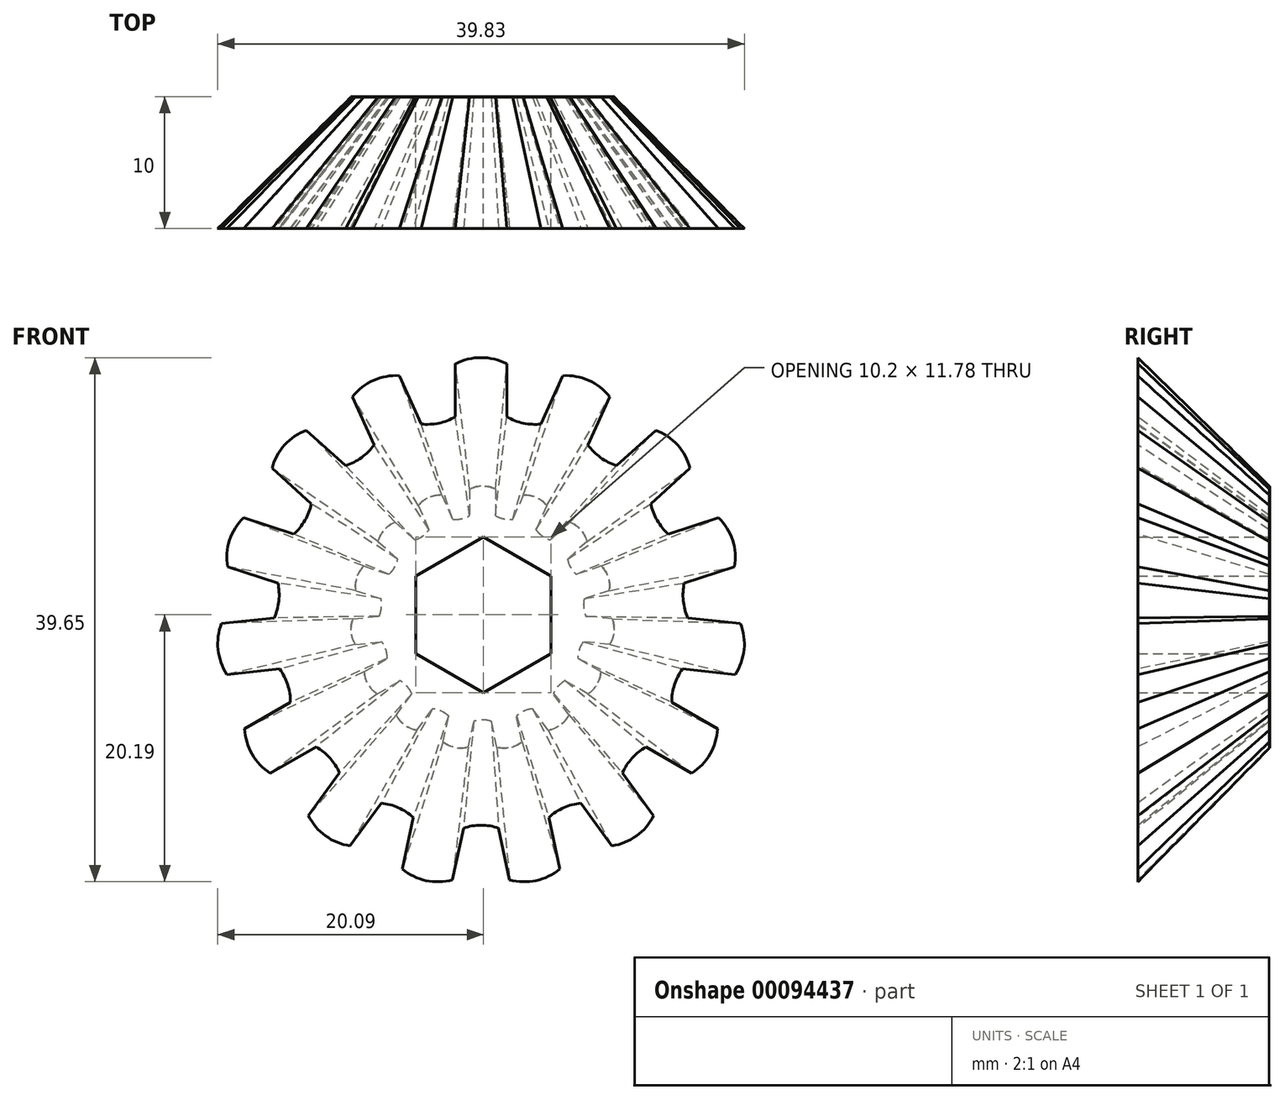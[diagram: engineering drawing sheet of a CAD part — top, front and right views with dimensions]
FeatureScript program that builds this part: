
annotation { "Feature Type Name" : "Feature", "Feature Type Description" : "" }
export const myFeature = defineFeature(function(context is Context, id is Id, definition is map)
    precondition{}
    {
        {
            var Q0;
            Q0=qCreatedBy(makeId("Front.planeOp"),FACE);
            cPlane(context, id + "F0", {"entities" : qUnion([Q0]), "cplaneType" : CPlaneType.OFFSET, "offset" : 10 * mm, "width" : 150 * mm, "height" : 150 * mm});
        }
        {
            var Q0;
            Q0=qCreatedBy(makeId("Front.planeOp"),FACE);
            var sketch = newSketch(context, id + "F1", { "sketchPlane" : qUnion([Q0])});
            skLineSegment(sketch, "E0", {"start": v(-2.07, 19.01) * mm, "end": v(-2.07, 15.01) * mm});
            skLineSegment(sketch, "E1.MirrorCS", {"start": v(1.81, 19.01) * mm, "end": v(1.81, 15.01) * mm});
            skArc(sketch, "E2", {"start": v(1.81, 19.01) * mm, "mid": v(-0.13, 19.49) * mm, "end": v(-2.07, 19.01) * mm});
            skLineSegment(sketch, "E3.1.0", {"start": v(-9.84, 16.54) * mm, "end": v(-8.22, 12.88) * mm});
            skArc(sketch, "E3.1.1", {"start": v(-6.3, 18.12) * mm, "mid": v(-8.26, 17.76) * mm, "end": v(-9.84, 16.54) * mm});
            skLineSegment(sketch, "E3.1.2", {"start": v(-6.3, 18.12) * mm, "end": v(-4.67, 14.46) * mm});
            skLineSegment(sketch, "E3.2.0", {"start": v(-15.94, 11.1) * mm, "end": v(-12.97, 8.43) * mm});
            skArc(sketch, "E3.2.1", {"start": v(-13.34, 14) * mm, "mid": v(-15, 12.87) * mm, "end": v(-15.94, 11.1) * mm});
            skLineSegment(sketch, "E3.2.2", {"start": v(-13.34, 14) * mm, "end": v(-10.37, 11.32) * mm});
            skLineSegment(sketch, "E3.3.0", {"start": v(-19.3, 3.67) * mm, "end": v(-15.5, 2.44) * mm});
            skArc(sketch, "E3.3.1", {"start": v(-18.1, 7.37) * mm, "mid": v(-19.15, 5.67) * mm, "end": v(-19.3, 3.67) * mm});
            skLineSegment(sketch, "E3.3.2", {"start": v(-18.1, 7.37) * mm, "end": v(-14.3, 6.13) * mm});
            skLineSegment(sketch, "E3.4.0", {"start": v(-19.34, -4.49) * mm, "end": v(-15.37, -4.07) * mm});
            skArc(sketch, "E3.4.1", {"start": v(-19.75, -0.62) * mm, "mid": v(-20.02, -2.6) * mm, "end": v(-19.34, -4.49) * mm});
            skLineSegment(sketch, "E3.4.2", {"start": v(-19.75, -0.62) * mm, "end": v(-15.77, -0.2) * mm});
            skLineSegment(sketch, "E3.5.0", {"start": v(-16.07, -11.96) * mm, "end": v(-12.6, -9.96) * mm});
            skArc(sketch, "E3.5.1", {"start": v(-18, -8.6) * mm, "mid": v(-17.45, -10.51) * mm, "end": v(-16.07, -11.96) * mm});
            skLineSegment(sketch, "E3.5.2", {"start": v(-18, -8.6) * mm, "end": v(-14.55, -6.6) * mm});
            skLineSegment(sketch, "E3.6.0", {"start": v(-10.03, -17.45) * mm, "end": v(-7.68, -14.21) * mm});
            skArc(sketch, "E3.6.1", {"start": v(-13.18, -15.17) * mm, "mid": v(-11.88, -16.7) * mm, "end": v(-10.03, -17.45) * mm});
            skLineSegment(sketch, "E3.6.2", {"start": v(-13.18, -15.17) * mm, "end": v(-10.83, -11.93) * mm});
            skLineSegment(sketch, "E3.7.0", {"start": v(-2.29, -20.01) * mm, "end": v(-1.46, -16.1) * mm});
            skArc(sketch, "E3.7.1", {"start": v(-6.09, -19.2) * mm, "mid": v(-4.29, -20.07) * mm, "end": v(-2.29, -20.01) * mm});
            skLineSegment(sketch, "E3.7.2", {"start": v(-6.09, -19.2) * mm, "end": v(-5.26, -15.3) * mm});
            skLineSegment(sketch, "E3.8.0", {"start": v(5.83, -19.2) * mm, "end": v(5, -15.3) * mm});
            skArc(sketch, "E3.8.1", {"start": v(2.03, -20.01) * mm, "mid": v(4.03, -20.07) * mm, "end": v(5.83, -19.2) * mm});
            skLineSegment(sketch, "E3.8.2", {"start": v(2.03, -20.01) * mm, "end": v(1.2, -16.1) * mm});
            skLineSegment(sketch, "E3.9.0", {"start": v(12.92, -15.17) * mm, "end": v(10.57, -11.93) * mm});
            skArc(sketch, "E3.9.1", {"start": v(9.78, -17.45) * mm, "mid": v(11.63, -16.7) * mm, "end": v(12.92, -15.17) * mm});
            skLineSegment(sketch, "E3.9.2", {"start": v(9.78, -17.45) * mm, "end": v(7.43, -14.21) * mm});
            skLineSegment(sketch, "E3.10.0", {"start": v(17.75, -8.6) * mm, "end": v(14.29, -6.6) * mm});
            skArc(sketch, "E3.10.1", {"start": v(15.81, -11.96) * mm, "mid": v(17.2, -10.51) * mm, "end": v(17.75, -8.6) * mm});
            skLineSegment(sketch, "E3.10.2", {"start": v(15.81, -11.96) * mm, "end": v(12.35, -9.96) * mm});
            skLineSegment(sketch, "E3.11.0", {"start": v(19.5, -0.62) * mm, "end": v(15.52, -0.2) * mm});
            skArc(sketch, "E3.11.1", {"start": v(19.09, -4.49) * mm, "mid": v(19.76, -2.6) * mm, "end": v(19.5, -0.62) * mm});
            skLineSegment(sketch, "E3.11.2", {"start": v(19.09, -4.49) * mm, "end": v(15.1, -4.07) * mm});
            skLineSegment(sketch, "E3.12.0", {"start": v(17.84, 7.37) * mm, "end": v(14.04, 6.13) * mm});
            skArc(sketch, "E3.12.1", {"start": v(19.04, 3.67) * mm, "mid": v(18.9, 5.67) * mm, "end": v(17.84, 7.37) * mm});
            skLineSegment(sketch, "E3.12.2", {"start": v(19.04, 3.67) * mm, "end": v(15.24, 2.44) * mm});
            skLineSegment(sketch, "E3.13.0", {"start": v(13.08, 14) * mm, "end": v(10.1, 11.32) * mm});
            skArc(sketch, "E3.13.1", {"start": v(15.68, 11.1) * mm, "mid": v(14.73, 12.87) * mm, "end": v(13.08, 14) * mm});
            skLineSegment(sketch, "E3.13.2", {"start": v(15.68, 11.1) * mm, "end": v(12.7, 8.43) * mm});
            skLineSegment(sketch, "E3.14.0", {"start": v(6.04, 18.12) * mm, "end": v(4.41, 14.46) * mm});
            skArc(sketch, "E3.14.1", {"start": v(9.59, 16.54) * mm, "mid": v(8, 17.76) * mm, "end": v(6.04, 18.12) * mm});
            skLineSegment(sketch, "E3.14.2", {"start": v(9.59, 16.54) * mm, "end": v(7.96, 12.88) * mm});
            skPoint(sketch, "E3.center", {"position": v(-0.13, -0.51) * mm});
            skArc(sketch, "E4", {"start": v(-4.67, 14.46) * mm, "mid": v(-3.32, 14.53) * mm, "end": v(-2.07, 15.01) * mm});
            skArc(sketch, "E5.1.0", {"start": v(-10.37, 11.32) * mm, "mid": v(-9.17, 11.93) * mm, "end": v(-8.22, 12.88) * mm});
            skArc(sketch, "E5.2.0", {"start": v(-14.3, 6.13) * mm, "mid": v(-13.44, 7.18) * mm, "end": v(-12.97, 8.43) * mm});
            skArc(sketch, "E5.3.0", {"start": v(-15.77, -0.2) * mm, "mid": v(-15.42, 1.1) * mm, "end": v(-15.5, 2.44) * mm});
            skArc(sketch, "E5.4.0", {"start": v(-14.55, -6.6) * mm, "mid": v(-14.75, -5.26) * mm, "end": v(-15.37, -4.07) * mm});
            skArc(sketch, "E5.5.0", {"start": v(-10.83, -11.93) * mm, "mid": v(-11.55, -10.8) * mm, "end": v(-12.6, -9.96) * mm});
            skArc(sketch, "E5.6.0", {"start": v(-5.26, -15.3) * mm, "mid": v(-6.38, -14.56) * mm, "end": v(-7.68, -14.21) * mm});
            skArc(sketch, "E5.7.0", {"start": v(1.2, -16.1) * mm, "mid": v(-0.13, -15.89) * mm, "end": v(-1.46, -16.1) * mm});
            skArc(sketch, "E5.8.0", {"start": v(7.43, -14.21) * mm, "mid": v(6.13, -14.56) * mm, "end": v(5, -15.3) * mm});
            skArc(sketch, "E5.9.0", {"start": v(12.35, -9.96) * mm, "mid": v(11.3, -10.8) * mm, "end": v(10.57, -11.93) * mm});
            skArc(sketch, "E5.10.0", {"start": v(15.1, -4.07) * mm, "mid": v(14.5, -5.26) * mm, "end": v(14.29, -6.6) * mm});
            skArc(sketch, "E5.11.0", {"start": v(15.24, 2.44) * mm, "mid": v(15.16, 1.1) * mm, "end": v(15.52, -0.2) * mm});
            skArc(sketch, "E5.12.0", {"start": v(12.7, 8.43) * mm, "mid": v(13.19, 7.18) * mm, "end": v(14.04, 6.13) * mm});
            skArc(sketch, "E5.13.0", {"start": v(7.96, 12.88) * mm, "mid": v(8.9, 11.93) * mm, "end": v(10.1, 11.32) * mm});
            skArc(sketch, "E5.14.0", {"start": v(1.81, 15.01) * mm, "mid": v(3.07, 14.53) * mm, "end": v(4.41, 14.46) * mm});
            skSolve(sketch);
        }
        {
            var Q0;
            Q0=qCreatedBy(id+"F0.planeOp",FACE);
            var sketch = newSketch(context, id + "F2", { "sketchPlane" : qUnion([Q0])});
            skLineSegment(sketch, "E6", {"start": v(-2.12, 18.99) * mm, "end": v(-2.12, 14.99) * mm});
            skLineSegment(sketch, "E7.MirrorCS", {"start": v(1.77, 18.99) * mm, "end": v(1.77, 14.99) * mm});
            skArc(sketch, "E8", {"start": v(1.77, 18.99) * mm, "mid": v(-0.18, 19.46) * mm, "end": v(-2.12, 18.99) * mm});
            skLineSegment(sketch, "E9.1.0", {"start": v(-9.9, 16.5) * mm, "end": v(-8.27, 12.85) * mm});
            skArc(sketch, "E9.1.1", {"start": v(-6.34, 18.09) * mm, "mid": v(-8.31, 17.73) * mm, "end": v(-9.9, 16.5) * mm});
            skLineSegment(sketch, "E9.1.2", {"start": v(-6.34, 18.09) * mm, "end": v(-4.72, 14.43) * mm});
            skLineSegment(sketch, "E9.2.0", {"start": v(-15.99, 11.08) * mm, "end": v(-13.02, 8.4) * mm});
            skArc(sketch, "E9.2.1", {"start": v(-13.39, 13.97) * mm, "mid": v(-15.04, 12.84) * mm, "end": v(-15.99, 11.08) * mm});
            skLineSegment(sketch, "E9.2.2", {"start": v(-13.39, 13.97) * mm, "end": v(-10.42, 11.3) * mm});
            skLineSegment(sketch, "E9.3.0", {"start": v(-19.35, 3.65) * mm, "end": v(-15.54, 2.41) * mm});
            skArc(sketch, "E9.3.1", {"start": v(-18.15, 7.34) * mm, "mid": v(-19.2, 5.64) * mm, "end": v(-19.35, 3.65) * mm});
            skLineSegment(sketch, "E9.3.2", {"start": v(-18.15, 7.34) * mm, "end": v(-14.34, 6.1) * mm});
            skLineSegment(sketch, "E9.4.0", {"start": v(-19.4, -4.51) * mm, "end": v(-15.42, -4.1) * mm});
            skArc(sketch, "E9.4.1", {"start": v(-19.8, -0.65) * mm, "mid": v(-20.07, -2.63) * mm, "end": v(-19.4, -4.51) * mm});
            skLineSegment(sketch, "E9.4.2", {"start": v(-19.8, -0.65) * mm, "end": v(-15.82, -0.23) * mm});
            skLineSegment(sketch, "E9.5.0", {"start": v(-16.12, -11.99) * mm, "end": v(-12.65, -9.99) * mm});
            skArc(sketch, "E9.5.1", {"start": v(-18.06, -8.62) * mm, "mid": v(-17.5, -10.54) * mm, "end": v(-16.12, -11.99) * mm});
            skLineSegment(sketch, "E9.5.2", {"start": v(-18.06, -8.62) * mm, "end": v(-14.6, -6.62) * mm});
            skLineSegment(sketch, "E9.6.0", {"start": v(-10.08, -17.48) * mm, "end": v(-7.73, -14.24) * mm});
            skArc(sketch, "E9.6.1", {"start": v(-13.23, -15.2) * mm, "mid": v(-11.93, -16.72) * mm, "end": v(-10.08, -17.48) * mm});
            skLineSegment(sketch, "E9.6.2", {"start": v(-13.23, -15.2) * mm, "end": v(-10.88, -11.96) * mm});
            skLineSegment(sketch, "E9.7.0", {"start": v(-2.34, -20.04) * mm, "end": v(-1.5, -16.13) * mm});
            skArc(sketch, "E9.7.1", {"start": v(-6.14, -19.23) * mm, "mid": v(-4.34, -20.1) * mm, "end": v(-2.34, -20.04) * mm});
            skLineSegment(sketch, "E9.7.2", {"start": v(-6.14, -19.23) * mm, "end": v(-5.3, -15.32) * mm});
            skLineSegment(sketch, "E9.8.0", {"start": v(5.78, -19.23) * mm, "end": v(4.95, -15.32) * mm});
            skArc(sketch, "E9.8.1", {"start": v(1.98, -20.04) * mm, "mid": v(3.98, -20.1) * mm, "end": v(5.78, -19.23) * mm});
            skLineSegment(sketch, "E9.8.2", {"start": v(1.98, -20.04) * mm, "end": v(1.15, -16.13) * mm});
            skLineSegment(sketch, "E9.9.0", {"start": v(12.87, -15.2) * mm, "end": v(10.52, -11.96) * mm});
            skArc(sketch, "E9.9.1", {"start": v(9.73, -17.48) * mm, "mid": v(11.58, -16.72) * mm, "end": v(12.87, -15.2) * mm});
            skLineSegment(sketch, "E9.9.2", {"start": v(9.73, -17.48) * mm, "end": v(7.38, -14.24) * mm});
            skLineSegment(sketch, "E9.10.0", {"start": v(17.7, -8.62) * mm, "end": v(14.24, -6.62) * mm});
            skArc(sketch, "E9.10.1", {"start": v(15.76, -11.99) * mm, "mid": v(17.14, -10.54) * mm, "end": v(17.7, -8.62) * mm});
            skLineSegment(sketch, "E9.10.2", {"start": v(15.76, -11.99) * mm, "end": v(12.3, -9.99) * mm});
            skLineSegment(sketch, "E9.11.0", {"start": v(19.44, -0.65) * mm, "end": v(15.47, -0.23) * mm});
            skArc(sketch, "E9.11.1", {"start": v(19.04, -4.51) * mm, "mid": v(19.71, -2.63) * mm, "end": v(19.44, -0.65) * mm});
            skLineSegment(sketch, "E9.11.2", {"start": v(19.04, -4.51) * mm, "end": v(15.06, -4.1) * mm});
            skLineSegment(sketch, "E9.12.0", {"start": v(17.8, 7.34) * mm, "end": v(13.99, 6.1) * mm});
            skArc(sketch, "E9.12.1", {"start": v(19, 3.65) * mm, "mid": v(18.84, 5.64) * mm, "end": v(17.8, 7.34) * mm});
            skLineSegment(sketch, "E9.12.2", {"start": v(19, 3.65) * mm, "end": v(15.19, 2.41) * mm});
            skLineSegment(sketch, "E9.13.0", {"start": v(13.03, 13.97) * mm, "end": v(10.06, 11.3) * mm});
            skArc(sketch, "E9.13.1", {"start": v(15.63, 11.08) * mm, "mid": v(14.69, 12.84) * mm, "end": v(13.03, 13.97) * mm});
            skLineSegment(sketch, "E9.13.2", {"start": v(15.63, 11.08) * mm, "end": v(12.66, 8.4) * mm});
            skLineSegment(sketch, "E9.14.0", {"start": v(5.99, 18.09) * mm, "end": v(4.36, 14.43) * mm});
            skArc(sketch, "E9.14.1", {"start": v(9.54, 16.5) * mm, "mid": v(7.96, 17.73) * mm, "end": v(5.99, 18.09) * mm});
            skLineSegment(sketch, "E9.14.2", {"start": v(9.54, 16.5) * mm, "end": v(7.91, 12.85) * mm});
            skPoint(sketch, "E9.center", {"position": v(-0.18, -0.54) * mm});
            skArc(sketch, "E10", {"start": v(-4.72, 14.43) * mm, "mid": v(-3.37, 14.5) * mm, "end": v(-2.12, 14.99) * mm});
            skArc(sketch, "E11.1.0", {"start": v(-10.42, 11.3) * mm, "mid": v(-9.22, 11.9) * mm, "end": v(-8.27, 12.85) * mm});
            skArc(sketch, "E11.2.0", {"start": v(-14.34, 6.1) * mm, "mid": v(-13.5, 7.15) * mm, "end": v(-13.02, 8.4) * mm});
            skArc(sketch, "E11.3.0", {"start": v(-15.82, -0.23) * mm, "mid": v(-15.47, 1.07) * mm, "end": v(-15.54, 2.41) * mm});
            skArc(sketch, "E11.4.0", {"start": v(-14.6, -6.62) * mm, "mid": v(-14.8, -5.3) * mm, "end": v(-15.42, -4.1) * mm});
            skArc(sketch, "E11.5.0", {"start": v(-10.88, -11.96) * mm, "mid": v(-11.6, -10.83) * mm, "end": v(-12.65, -9.99) * mm});
            skArc(sketch, "E11.6.0", {"start": v(-5.3, -15.32) * mm, "mid": v(-6.43, -14.59) * mm, "end": v(-7.73, -14.24) * mm});
            skArc(sketch, "E11.7.0", {"start": v(1.15, -16.13) * mm, "mid": v(-0.18, -15.92) * mm, "end": v(-1.5, -16.13) * mm});
            skArc(sketch, "E11.8.0", {"start": v(7.38, -14.24) * mm, "mid": v(6.08, -14.59) * mm, "end": v(4.95, -15.32) * mm});
            skArc(sketch, "E11.9.0", {"start": v(12.3, -9.99) * mm, "mid": v(11.25, -10.83) * mm, "end": v(10.52, -11.96) * mm});
            skArc(sketch, "E11.10.0", {"start": v(15.06, -4.1) * mm, "mid": v(14.45, -5.3) * mm, "end": v(14.24, -6.62) * mm});
            skArc(sketch, "E11.11.0", {"start": v(15.19, 2.41) * mm, "mid": v(15.11, 1.07) * mm, "end": v(15.47, -0.23) * mm});
            skArc(sketch, "E11.12.0", {"start": v(12.66, 8.4) * mm, "mid": v(13.14, 7.15) * mm, "end": v(13.99, 6.1) * mm});
            skArc(sketch, "E11.13.0", {"start": v(7.91, 12.85) * mm, "mid": v(8.86, 11.9) * mm, "end": v(10.06, 11.3) * mm});
            skArc(sketch, "E11.14.0", {"start": v(1.77, 14.99) * mm, "mid": v(3.02, 14.5) * mm, "end": v(4.36, 14.43) * mm});
            skSolve(sketch);
        }
        {
            var Q0;
            Q0 = qSketchRegion(id + "F1", true);
            extrude(context, id + "F3", {"entities" : qUnion([Q0]), "depth" : 0.1 * mm});
        }
        {
            var Q0;
            Q0=makeQuery(id+"F3.opExtrude","SWEPT_BODY",BODY,{"disambiguationData":[OSD([sQuery(id+"F1.wireOp",EDGE,"E0"),sQuery(id+"F1.wireOp",EDGE,"E1.MirrorCS"),sQuery(id+"F1.wireOp",EDGE,"E2"),sQuery(id+"F1.wireOp",EDGE,"E3.1.0"),sQuery(id+"F1.wireOp",EDGE,"E3.1.1"),sQuery(id+"F1.wireOp",EDGE,"E3.1.2"),sQuery(id+"F1.wireOp",EDGE,"E3.2.0"),sQuery(id+"F1.wireOp",EDGE,"E3.2.1"),sQuery(id+"F1.wireOp",EDGE,"E3.2.2"),sQuery(id+"F1.wireOp",EDGE,"E3.3.0"),sQuery(id+"F1.wireOp",EDGE,"E3.3.1"),sQuery(id+"F1.wireOp",EDGE,"E3.3.2"),sQuery(id+"F1.wireOp",EDGE,"E3.4.0"),sQuery(id+"F1.wireOp",EDGE,"E3.4.1"),sQuery(id+"F1.wireOp",EDGE,"E3.4.2"),sQuery(id+"F1.wireOp",EDGE,"E3.5.0"),sQuery(id+"F1.wireOp",EDGE,"E3.5.1"),sQuery(id+"F1.wireOp",EDGE,"E3.5.2"),sQuery(id+"F1.wireOp",EDGE,"E3.6.0"),sQuery(id+"F1.wireOp",EDGE,"E3.6.1"),sQuery(id+"F1.wireOp",EDGE,"E3.6.2"),sQuery(id+"F1.wireOp",EDGE,"E3.7.0"),sQuery(id+"F1.wireOp",EDGE,"E3.7.1"),sQuery(id+"F1.wireOp",EDGE,"E3.7.2"),sQuery(id+"F1.wireOp",EDGE,"E3.8.0"),sQuery(id+"F1.wireOp",EDGE,"E3.8.1"),sQuery(id+"F1.wireOp",EDGE,"E3.8.2"),sQuery(id+"F1.wireOp",EDGE,"E3.9.0"),sQuery(id+"F1.wireOp",EDGE,"E3.9.1"),sQuery(id+"F1.wireOp",EDGE,"E3.9.2"),sQuery(id+"F1.wireOp",EDGE,"E3.10.0"),sQuery(id+"F1.wireOp",EDGE,"E3.10.1"),sQuery(id+"F1.wireOp",EDGE,"E3.10.2"),sQuery(id+"F1.wireOp",EDGE,"E3.11.0"),sQuery(id+"F1.wireOp",EDGE,"E3.11.1"),sQuery(id+"F1.wireOp",EDGE,"E3.11.2"),sQuery(id+"F1.wireOp",EDGE,"E3.12.0"),sQuery(id+"F1.wireOp",EDGE,"E3.12.1"),sQuery(id+"F1.wireOp",EDGE,"E3.12.2"),sQuery(id+"F1.wireOp",EDGE,"E3.13.0"),sQuery(id+"F1.wireOp",EDGE,"E3.13.1"),sQuery(id+"F1.wireOp",EDGE,"E3.13.2"),sQuery(id+"F1.wireOp",EDGE,"E3.14.0"),sQuery(id+"F1.wireOp",EDGE,"E3.14.1"),sQuery(id+"F1.wireOp",EDGE,"E3.14.2"),sQuery(id+"F1.wireOp",EDGE,"E4"),sQuery(id+"F1.wireOp",EDGE,"E5.1.0"),sQuery(id+"F1.wireOp",EDGE,"E5.2.0"),sQuery(id+"F1.wireOp",EDGE,"E5.3.0"),sQuery(id+"F1.wireOp",EDGE,"E5.4.0"),sQuery(id+"F1.wireOp",EDGE,"E5.5.0"),sQuery(id+"F1.wireOp",EDGE,"E5.6.0"),sQuery(id+"F1.wireOp",EDGE,"E5.7.0"),sQuery(id+"F1.wireOp",EDGE,"E5.8.0"),sQuery(id+"F1.wireOp",EDGE,"E5.9.0"),sQuery(id+"F1.wireOp",EDGE,"E5.10.0"),sQuery(id+"F1.wireOp",EDGE,"E5.11.0"),sQuery(id+"F1.wireOp",EDGE,"E5.12.0"),sQuery(id+"F1.wireOp",EDGE,"E5.13.0"),sQuery(id+"F1.wireOp",EDGE,"E5.14.0")])]});
            var Q1;
            Q1=qCreatedBy(makeId("Origin.pointOp"),VERTEX);
            transform(context, id + "F4", {"entities" : qUnion([Q0]), "transformType" : TransformType.SCALE_UNIFORMLY, "scale" : 0.5, "scalePoint" : qUnion([Q1]), "makeCopy" : false});
        }
        {
            var Q1;
            Q1=makeQuery(id+"F3.opExtrude","CAP_FACE",FACE,{"disambiguationData":[OSD([sQuery(id+"F1.wireOp",EDGE,"E0"),sQuery(id+"F1.wireOp",EDGE,"E1.MirrorCS"),sQuery(id+"F1.wireOp",EDGE,"E2"),sQuery(id+"F1.wireOp",EDGE,"E3.1.0"),sQuery(id+"F1.wireOp",EDGE,"E3.1.1"),sQuery(id+"F1.wireOp",EDGE,"E3.1.2"),sQuery(id+"F1.wireOp",EDGE,"E3.2.0"),sQuery(id+"F1.wireOp",EDGE,"E3.2.1"),sQuery(id+"F1.wireOp",EDGE,"E3.2.2"),sQuery(id+"F1.wireOp",EDGE,"E3.3.0"),sQuery(id+"F1.wireOp",EDGE,"E3.3.1"),sQuery(id+"F1.wireOp",EDGE,"E3.3.2"),sQuery(id+"F1.wireOp",EDGE,"E3.4.0"),sQuery(id+"F1.wireOp",EDGE,"E3.4.1"),sQuery(id+"F1.wireOp",EDGE,"E3.4.2"),sQuery(id+"F1.wireOp",EDGE,"E3.5.0"),sQuery(id+"F1.wireOp",EDGE,"E3.5.1"),sQuery(id+"F1.wireOp",EDGE,"E3.5.2"),sQuery(id+"F1.wireOp",EDGE,"E3.6.0"),sQuery(id+"F1.wireOp",EDGE,"E3.6.1"),sQuery(id+"F1.wireOp",EDGE,"E3.6.2"),sQuery(id+"F1.wireOp",EDGE,"E3.7.0"),sQuery(id+"F1.wireOp",EDGE,"E3.7.1"),sQuery(id+"F1.wireOp",EDGE,"E3.7.2"),sQuery(id+"F1.wireOp",EDGE,"E3.8.0"),sQuery(id+"F1.wireOp",EDGE,"E3.8.1"),sQuery(id+"F1.wireOp",EDGE,"E3.8.2"),sQuery(id+"F1.wireOp",EDGE,"E3.9.0"),sQuery(id+"F1.wireOp",EDGE,"E3.9.1"),sQuery(id+"F1.wireOp",EDGE,"E3.9.2"),sQuery(id+"F1.wireOp",EDGE,"E3.10.0"),sQuery(id+"F1.wireOp",EDGE,"E3.10.1"),sQuery(id+"F1.wireOp",EDGE,"E3.10.2"),sQuery(id+"F1.wireOp",EDGE,"E3.11.0"),sQuery(id+"F1.wireOp",EDGE,"E3.11.1"),sQuery(id+"F1.wireOp",EDGE,"E3.11.2"),sQuery(id+"F1.wireOp",EDGE,"E3.12.0"),sQuery(id+"F1.wireOp",EDGE,"E3.12.1"),sQuery(id+"F1.wireOp",EDGE,"E3.12.2"),sQuery(id+"F1.wireOp",EDGE,"E3.13.0"),sQuery(id+"F1.wireOp",EDGE,"E3.13.1"),sQuery(id+"F1.wireOp",EDGE,"E3.13.2"),sQuery(id+"F1.wireOp",EDGE,"E3.14.0"),sQuery(id+"F1.wireOp",EDGE,"E3.14.1"),sQuery(id+"F1.wireOp",EDGE,"E3.14.2"),sQuery(id+"F1.wireOp",EDGE,"E4"),sQuery(id+"F1.wireOp",EDGE,"E5.1.0"),sQuery(id+"F1.wireOp",EDGE,"E5.2.0"),sQuery(id+"F1.wireOp",EDGE,"E5.3.0"),sQuery(id+"F1.wireOp",EDGE,"E5.4.0"),sQuery(id+"F1.wireOp",EDGE,"E5.5.0"),sQuery(id+"F1.wireOp",EDGE,"E5.6.0"),sQuery(id+"F1.wireOp",EDGE,"E5.7.0"),sQuery(id+"F1.wireOp",EDGE,"E5.8.0"),sQuery(id+"F1.wireOp",EDGE,"E5.9.0"),sQuery(id+"F1.wireOp",EDGE,"E5.10.0"),sQuery(id+"F1.wireOp",EDGE,"E5.11.0"),sQuery(id+"F1.wireOp",EDGE,"E5.12.0"),sQuery(id+"F1.wireOp",EDGE,"E5.13.0"),sQuery(id+"F1.wireOp",EDGE,"E5.14.0")])],"isStart":false});
            var Q2;
            Q2=makeQuery(id+"F2.imprint","IMPRINT",FACE,{"disambiguationData":[TD([[makeQuery(id+"F2.imprint","IMPRINT",EDGE,{"derivedFrom":sQuery(id+"F2.wireOp",EDGE,"E6")}),1.0]])]});
            loft(context, id + "F5", {"operationType" : NewBodyOperationType.ADD, "sheetProfilesArray" : [{ "sheetProfileEntities" : qUnion([Q1]) }, { "sheetProfileEntities" : qUnion([Q2]) }]});
        }
        {
            var Q0;
            Q0=makeQuery(id+"F3.opExtrude","CAP_FACE",FACE,{"disambiguationData":[OSD([sQuery(id+"F1.wireOp",EDGE,"E0"),sQuery(id+"F1.wireOp",EDGE,"E1.MirrorCS"),sQuery(id+"F1.wireOp",EDGE,"E2"),sQuery(id+"F1.wireOp",EDGE,"E3.1.0"),sQuery(id+"F1.wireOp",EDGE,"E3.1.1"),sQuery(id+"F1.wireOp",EDGE,"E3.1.2"),sQuery(id+"F1.wireOp",EDGE,"E3.2.0"),sQuery(id+"F1.wireOp",EDGE,"E3.2.1"),sQuery(id+"F1.wireOp",EDGE,"E3.2.2"),sQuery(id+"F1.wireOp",EDGE,"E3.3.0"),sQuery(id+"F1.wireOp",EDGE,"E3.3.1"),sQuery(id+"F1.wireOp",EDGE,"E3.3.2"),sQuery(id+"F1.wireOp",EDGE,"E3.4.0"),sQuery(id+"F1.wireOp",EDGE,"E3.4.1"),sQuery(id+"F1.wireOp",EDGE,"E3.4.2"),sQuery(id+"F1.wireOp",EDGE,"E3.5.0"),sQuery(id+"F1.wireOp",EDGE,"E3.5.1"),sQuery(id+"F1.wireOp",EDGE,"E3.5.2"),sQuery(id+"F1.wireOp",EDGE,"E3.6.0"),sQuery(id+"F1.wireOp",EDGE,"E3.6.1"),sQuery(id+"F1.wireOp",EDGE,"E3.6.2"),sQuery(id+"F1.wireOp",EDGE,"E3.7.0"),sQuery(id+"F1.wireOp",EDGE,"E3.7.1"),sQuery(id+"F1.wireOp",EDGE,"E3.7.2"),sQuery(id+"F1.wireOp",EDGE,"E3.8.0"),sQuery(id+"F1.wireOp",EDGE,"E3.8.1"),sQuery(id+"F1.wireOp",EDGE,"E3.8.2"),sQuery(id+"F1.wireOp",EDGE,"E3.9.0"),sQuery(id+"F1.wireOp",EDGE,"E3.9.1"),sQuery(id+"F1.wireOp",EDGE,"E3.9.2"),sQuery(id+"F1.wireOp",EDGE,"E3.10.0"),sQuery(id+"F1.wireOp",EDGE,"E3.10.1"),sQuery(id+"F1.wireOp",EDGE,"E3.10.2"),sQuery(id+"F1.wireOp",EDGE,"E3.11.0"),sQuery(id+"F1.wireOp",EDGE,"E3.11.1"),sQuery(id+"F1.wireOp",EDGE,"E3.11.2"),sQuery(id+"F1.wireOp",EDGE,"E3.12.0"),sQuery(id+"F1.wireOp",EDGE,"E3.12.1"),sQuery(id+"F1.wireOp",EDGE,"E3.12.2"),sQuery(id+"F1.wireOp",EDGE,"E3.13.0"),sQuery(id+"F1.wireOp",EDGE,"E3.13.1"),sQuery(id+"F1.wireOp",EDGE,"E3.13.2"),sQuery(id+"F1.wireOp",EDGE,"E3.14.0"),sQuery(id+"F1.wireOp",EDGE,"E3.14.1"),sQuery(id+"F1.wireOp",EDGE,"E3.14.2"),sQuery(id+"F1.wireOp",EDGE,"E4"),sQuery(id+"F1.wireOp",EDGE,"E5.1.0"),sQuery(id+"F1.wireOp",EDGE,"E5.2.0"),sQuery(id+"F1.wireOp",EDGE,"E5.3.0"),sQuery(id+"F1.wireOp",EDGE,"E5.4.0"),sQuery(id+"F1.wireOp",EDGE,"E5.5.0"),sQuery(id+"F1.wireOp",EDGE,"E5.6.0"),sQuery(id+"F1.wireOp",EDGE,"E5.7.0"),sQuery(id+"F1.wireOp",EDGE,"E5.8.0"),sQuery(id+"F1.wireOp",EDGE,"E5.9.0"),sQuery(id+"F1.wireOp",EDGE,"E5.10.0"),sQuery(id+"F1.wireOp",EDGE,"E5.11.0"),sQuery(id+"F1.wireOp",EDGE,"E5.12.0"),sQuery(id+"F1.wireOp",EDGE,"E5.13.0"),sQuery(id+"F1.wireOp",EDGE,"E5.14.0")])],"isStart":true});
            var sketch = newSketch(context, id + "F6", { "sketchPlane" : qUnion([Q0])});
            skPoint(sketch, "E12.cCircle.perimeterSnap0", {"position": v(4.13, 8.88) * mm});
            skPoint(sketch, "E12.0.midPoint.positionSnap0", {"position": v(4.13, 8.88) * mm});
            skCircle(sketch, "E13.cCircle", {"center": v(0, 0) * mm, "radius": 5.1 * mm, "construction": true});
            skLineSegment(sketch, "E13.0", {"start": v(5.1, 2.94) * mm, "end": v(5.1, -2.94) * mm});
            skLineSegment(sketch, "E13.1", {"start": v(5.1, -2.94) * mm, "end": v(0, -5.89) * mm});
            skLineSegment(sketch, "E13.2", {"start": v(0, -5.89) * mm, "end": v(-5.1, -2.94) * mm});
            skLineSegment(sketch, "E13.3", {"start": v(-5.1, -2.94) * mm, "end": v(-5.1, 2.94) * mm});
            skLineSegment(sketch, "E13.4", {"start": v(-5.1, 2.94) * mm, "end": v(0, 5.89) * mm});
            skLineSegment(sketch, "E13.5", {"start": v(0, 5.89) * mm, "end": v(5.1, 2.94) * mm});
            skPoint(sketch, "E13.0.midPoint", {"position": v(5.1, 0) * mm});
            skSolve(sketch);
        }
        {
            var Q0;
            Q0 = qSketchRegion(id + "F6", true);
            extrude(context, id + "F7", {"entities" : qUnion([Q0]), "operationType" : NewBodyOperationType.REMOVE, "endBound" : BoundingType.THROUGH_ALL, "oppositeDirection" : true, "depth" : 25 * mm});
        }
    });
